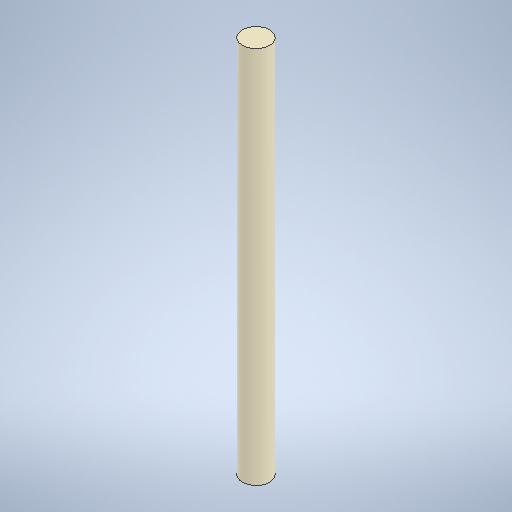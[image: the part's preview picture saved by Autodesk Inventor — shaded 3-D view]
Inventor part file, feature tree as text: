
AUTODESK INVENTOR PART (.ipt)
format: ipt  version: 2025.2 (Build 292293000, 293)  size: 232,448 bytes
history: native  units: in
note: dims shown in document units (in); Inventor stores cm internally (conversion verified against a paired STEP export)
features: extrude x1, sketch x1
ambient origin geometry x8: Origin, YZ Plane, XZ Plane, XY Plane, X Axis, Y Axis, Z Axis, Center Point
bodies: Solid1 (feature_tree)
feature tree (2):
  extrude  "Extrusion1"  Depth=7.0in TaperAngle=0.0deg
  sketch  "Sketch1"  dims[d0=0.5in d1=7.0in d2=0.0in]
